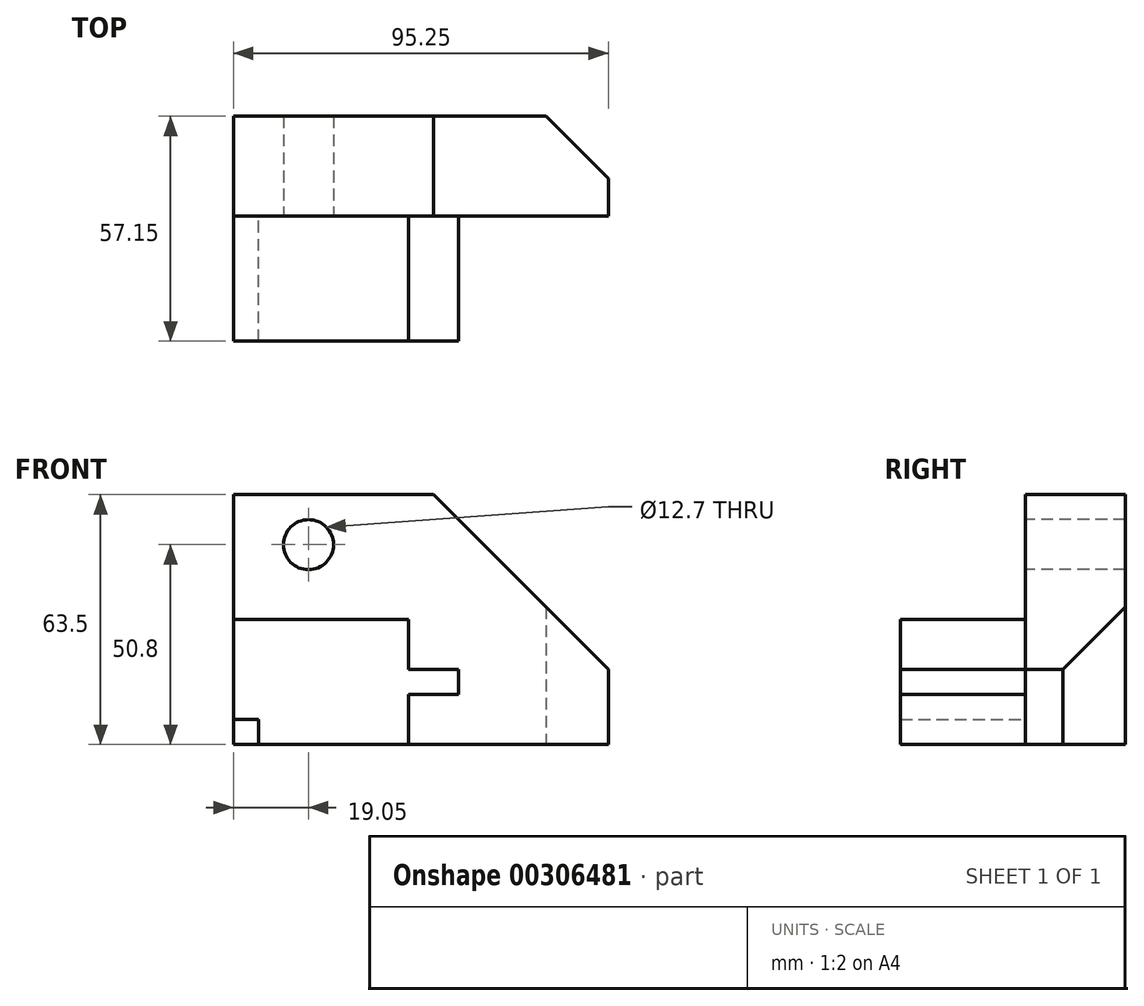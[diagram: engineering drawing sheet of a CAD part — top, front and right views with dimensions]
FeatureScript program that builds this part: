
annotation { "Feature Type Name" : "Feature", "Feature Type Description" : "" }
export const myFeature = defineFeature(function(context is Context, id is Id, definition is map)
    precondition{}
    {
        {
            var Q0;
            Q0=qCreatedBy(makeId("Front.planeOp"),FACE);
            var sketch = newSketch(context, id + "F0", { "sketchPlane" : qUnion([Q0])});
            skLineSegment(sketch, "E0", {"start": v(0, 0) * mm, "end": v(0, 63.5) * mm});
            skLineSegment(sketch, "E1", {"start": v(0, 63.5) * mm, "end": v(95.25, 63.5) * mm});
            skLineSegment(sketch, "E2", {"start": v(95.25, 63.5) * mm, "end": v(95.25, 0) * mm});
            skLineSegment(sketch, "E3", {"start": v(95.25, 0) * mm, "end": v(0, 0) * mm});
            skSolve(sketch);
        }
        {
            var Q0;
            Q0 = qSketchRegion(id + "F0", true);
            extrude(context, id + "F1", {"entities" : qUnion([Q0]), "depth" : 25.4 * mm});
        }
        {
            var Q0;
            Q0=makeQuery(id+"F1.opExtrude","CAP_FACE",FACE,{"disambiguationData":[OSD([sQuery(id+"F0.wireOp",EDGE,"E0"),sQuery(id+"F0.wireOp",EDGE,"E1"),sQuery(id+"F0.wireOp",EDGE,"E2"),sQuery(id+"F0.wireOp",EDGE,"E3")])],"isStart":false});
            var sketch = newSketch(context, id + "F2", { "sketchPlane" : qUnion([Q0])});
            skLineSegment(sketch, "E4", {"start": v(50.8, 63.5) * mm, "end": v(95.25, 19.05) * mm});
            skLineSegment(sketch, "E5", {"start": v(95.25, 19.05) * mm, "end": v(95.25, 63.5) * mm});
            skLineSegment(sketch, "E6", {"start": v(95.25, 63.5) * mm, "end": v(50.8, 63.5) * mm});
            skSolve(sketch);
        }
        {
            var Q0;
            Q0=makeQuery(id+"F2.imprint","IMPRINT",FACE,{"disambiguationData":[TD([[makeQuery(id+"F2.imprint","IMPRINT",EDGE,{"derivedFrom":sQuery(id+"F2.wireOp",EDGE,"E4")}),1.0]])]});
            extrude(context, id + "F3", {"entities" : qUnion([Q0]), "operationType" : NewBodyOperationType.REMOVE, "endBound" : BoundingType.THROUGH_ALL, "oppositeDirection" : true, "depth" : 25.4 * mm});
        }
        {
            var Q0;
            Q0=makeQuery(id+"F1.opExtrude","SWEPT_FACE",FACE,{"disambiguationData":[OSD([sQuery(id+"F0.wireOp",EDGE,"E3")])]});
            var sketch = newSketch(context, id + "F4", { "sketchPlane" : qUnion([Q0])});
            skLineSegment(sketch, "E7", {"start": v(95.25, 15.88) * mm, "end": v(79.37, 0) * mm});
            skLineSegment(sketch, "E8", {"start": v(79.37, 0) * mm, "end": v(95.25, 0) * mm});
            skLineSegment(sketch, "E9", {"start": v(95.25, 0) * mm, "end": v(95.25, 15.88) * mm});
            skSolve(sketch);
        }
        {
            var Q0;
            Q0=makeQuery(id+"F4.imprint","IMPRINT",FACE,{"disambiguationData":[TD([[makeQuery(id+"F4.imprint","IMPRINT",EDGE,{"derivedFrom":sQuery(id+"F4.wireOp",EDGE,"E7")}),1.0]])]});
            extrude(context, id + "F5", {"entities" : qUnion([Q0]), "operationType" : NewBodyOperationType.REMOVE, "endBound" : BoundingType.THROUGH_ALL, "oppositeDirection" : true, "depth" : 25.4 * mm});
        }
        {
            var Q0;
            Q0=makeQuery(id+"F1.opExtrude","CAP_FACE",FACE,{"disambiguationData":[OSD([sQuery(id+"F0.wireOp",EDGE,"E0"),sQuery(id+"F0.wireOp",EDGE,"E1"),sQuery(id+"F0.wireOp",EDGE,"E2"),sQuery(id+"F0.wireOp",EDGE,"E3")])],"isStart":false});
            var sketch = newSketch(context, id + "F6", { "sketchPlane" : qUnion([Q0])});
            skCircle(sketch, "E10", {"center": v(19.05, 50.8) * mm, "radius": 6.35 * mm});
            skSolve(sketch);
        }
        {
            var Q0;
            Q0 = qSketchRegion(id + "F6", true);
            extrude(context, id + "F7", {"entities" : qUnion([Q0]), "operationType" : NewBodyOperationType.REMOVE, "endBound" : BoundingType.THROUGH_ALL, "oppositeDirection" : true, "depth" : 25.4 * mm});
        }
        {
            var Q0;
            Q0=makeQuery(id+"F1.opExtrude","CAP_FACE",FACE,{"disambiguationData":[OSD([sQuery(id+"F0.wireOp",EDGE,"E0"),sQuery(id+"F0.wireOp",EDGE,"E1"),sQuery(id+"F0.wireOp",EDGE,"E2"),sQuery(id+"F0.wireOp",EDGE,"E3")])],"isStart":false});
            var sketch = newSketch(context, id + "F8", { "sketchPlane" : qUnion([Q0])});
            skLineSegment(sketch, "E11", {"start": v(0, 6.35) * mm, "end": v(0, 31.75) * mm});
            skLineSegment(sketch, "E12", {"start": v(0, 31.75) * mm, "end": v(44.45, 31.75) * mm});
            skLineSegment(sketch, "E13", {"start": v(44.45, 31.75) * mm, "end": v(44.45, 19.05) * mm});
            skLineSegment(sketch, "E14", {"start": v(44.45, 19.05) * mm, "end": v(57.15, 19.05) * mm});
            skLineSegment(sketch, "E15", {"start": v(57.15, 19.05) * mm, "end": v(57.15, 12.7) * mm});
            skLineSegment(sketch, "E16", {"start": v(57.15, 12.7) * mm, "end": v(44.45, 12.7) * mm});
            skLineSegment(sketch, "E17", {"start": v(44.45, 12.7) * mm, "end": v(44.45, 0) * mm});
            skLineSegment(sketch, "E18", {"start": v(44.45, 0) * mm, "end": v(6.35, 0) * mm});
            skLineSegment(sketch, "E19", {"start": v(6.35, 0) * mm, "end": v(6.35, 6.35) * mm});
            skLineSegment(sketch, "E20", {"start": v(6.35, 6.35) * mm, "end": v(0, 6.35) * mm});
            skSolve(sketch);
        }
        {
            var Q0;
            Q0 = qSketchRegion(id + "F8", true);
            extrude(context, id + "F9", {"entities" : qUnion([Q0]), "operationType" : NewBodyOperationType.ADD, "depth" : 31.75 * mm});
        }
    });
